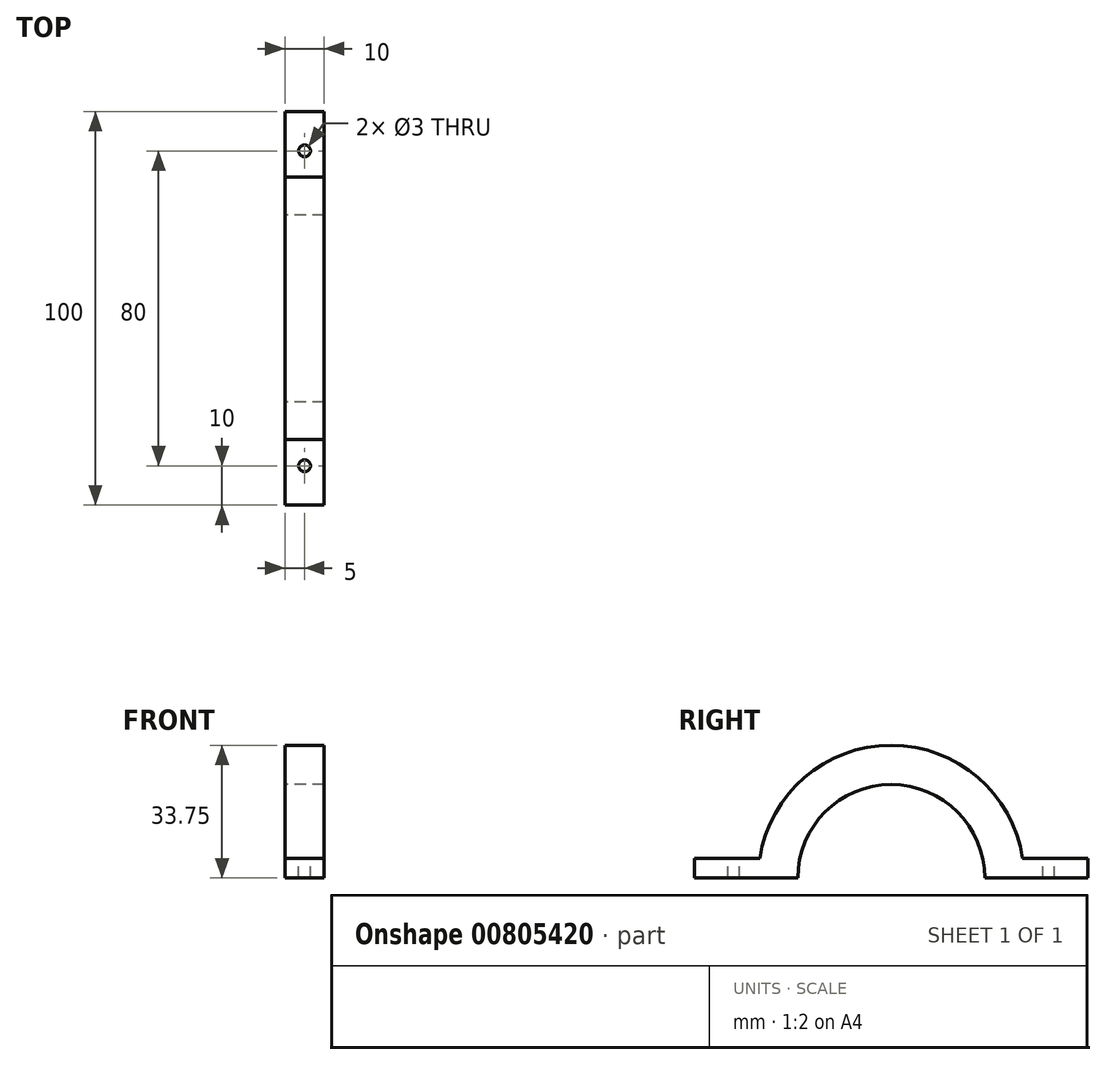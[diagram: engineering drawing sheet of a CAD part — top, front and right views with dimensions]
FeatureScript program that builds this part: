
annotation { "Feature Type Name" : "Feature", "Feature Type Description" : "" }
export const myFeature = defineFeature(function(context is Context, id is Id, definition is map)
    precondition{}
    {
        {
            var Q0;
            Q0=qCreatedBy(makeId("Right.planeOp"),FACE);
            var sketch = newSketch(context, id + "F0", { "sketchPlane" : qUnion([Q0])});
            skArc(sketch, "E0", {"start": v(-23.75, 0) * mm, "mid": v(0, 23.75) * mm, "end": v(23.75, 0) * mm});
            skArc(sketch, "E1", {"start": v(-33.38, 5) * mm, "mid": v(0, 33.75) * mm, "end": v(33.38, 5) * mm});
            skLineSegment(sketch, "E2.top", {"start": v(-50, 5) * mm, "end": v(-33.38, 5) * mm});
            skLineSegment(sketch, "E2.left", {"start": v(-50, 0) * mm, "end": v(-50, 5) * mm});
            skLineSegment(sketch, "E2.right", {"start": v(50, 0) * mm, "end": v(50, 5) * mm});
            skLineSegment(sketch, "E3", {"start": v(-50, 0) * mm, "end": v(-23.75, 0) * mm});
            skPoint(sketch, "E4.orphan", {"position": v(-50, -5) * mm});
            skPoint(sketch, "E5.orphan", {"position": v(50, -5) * mm});
            skLineSegment(sketch, "E6.trimOffspring", {"start": v(33.38, 5) * mm, "end": v(50, 5) * mm});
            skLineSegment(sketch, "E7.trimOffspring", {"start": v(23.75, 0) * mm, "end": v(50, 0) * mm});
            skPoint(sketch, "E8.orphan", {"position": v(-33.75, 0) * mm});
            skPoint(sketch, "E9.orphan", {"position": v(33.75, 0) * mm});
            skSolve(sketch);
        }
        {
            var Q0;
            Q0 = qSketchRegion(id + "F0", true);
            extrude(context, id + "F1", {"entities" : qUnion([Q0]), "depth" : 10 * mm, "offsetDistance" : 25 * mm});
        }
        {
            var Q0;
            Q0=makeQuery(id+"F1.opExtrude","SWEPT_FACE",FACE,{"disambiguationData":[OSD([sQuery(id+"F0.wireOp",EDGE,"E2.top")])]});
            var sketch = newSketch(context, id + "F2", { "sketchPlane" : qUnion([Q0])});
            skPoint(sketch, "E10.0", {"position": v(5, 50) * mm});
            skPoint(sketch, "E11.0", {"position": v(5, -50) * mm});
            skLineSegment(sketch, "E12", {"start": v(5, 50) * mm, "end": v(5, -50) * mm, "construction": true});
            skCircle(sketch, "E13", {"center": v(5, 40) * mm, "radius": 1.5 * mm});
            skCircle(sketch, "E14.MirrorC", {"center": v(5, -40) * mm, "radius": 1.5 * mm});
            skSolve(sketch);
        }
        {
            var Q0;
            Q0 = qSketchRegion(id + "F2", true);
            extrude(context, id + "F3", {"entities" : qUnion([Q0]), "operationType" : NewBodyOperationType.REMOVE, "oppositeDirection" : true, "depth" : 25 * mm, "offsetDistance" : 25 * mm});
        }
    });
